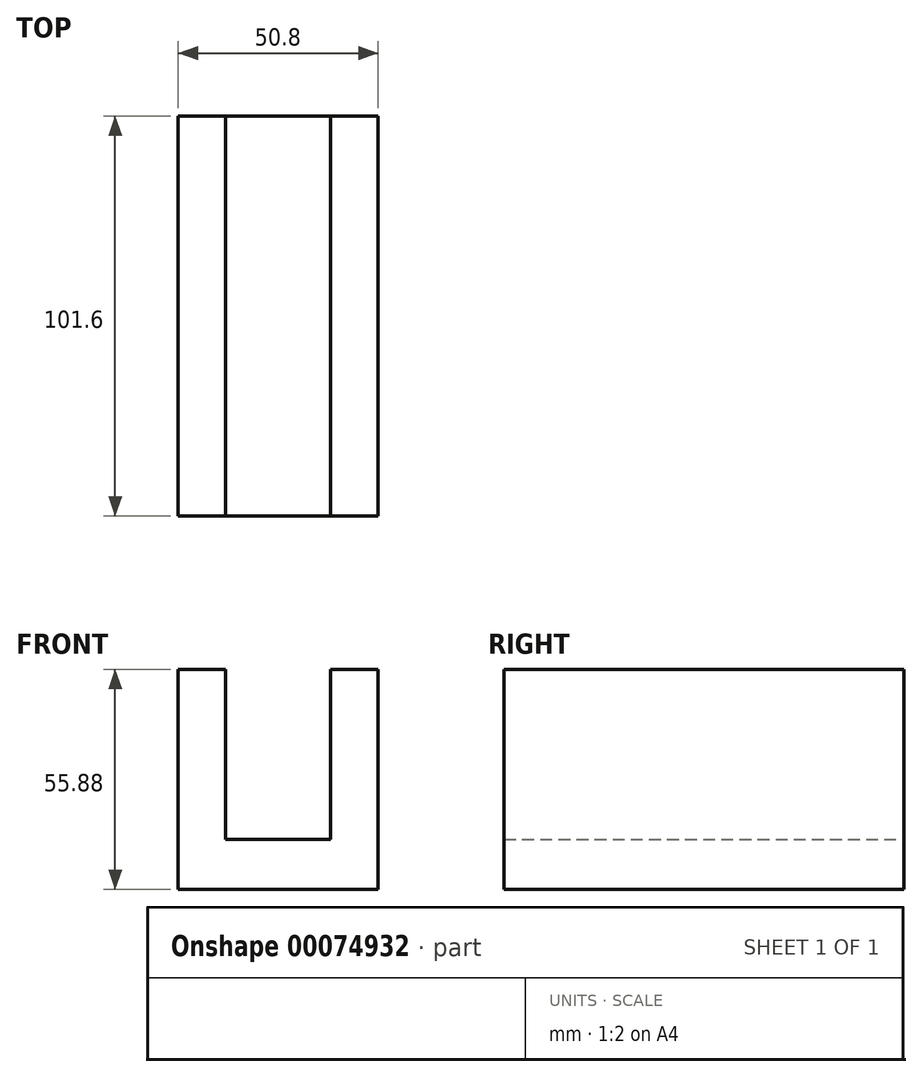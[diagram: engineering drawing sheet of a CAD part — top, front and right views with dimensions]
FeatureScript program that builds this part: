
annotation { "Feature Type Name" : "Feature", "Feature Type Description" : "" }
export const myFeature = defineFeature(function(context is Context, id is Id, definition is map)
    precondition{}
    {
        {
            var Q0;
            Q0=qCreatedBy(makeId("Top.planeOp"),FACE);
            var sketch = newSketch(context, id + "F0", { "sketchPlane" : qUnion([Q0])});
            skLineSegment(sketch, "E0.rect.bottom", {"start": v(25.4, -50.8) * mm, "end": v(-25.4, -50.8) * mm});
            skLineSegment(sketch, "E0.rect.top", {"start": v(25.4, 50.8) * mm, "end": v(-25.4, 50.8) * mm});
            skLineSegment(sketch, "E0.rect.left", {"start": v(25.4, -50.8) * mm, "end": v(25.4, 50.8) * mm});
            skLineSegment(sketch, "E0.rect.right", {"start": v(-25.4, -50.8) * mm, "end": v(-25.4, 50.8) * mm});
            skPoint(sketch, "E0.rect.middle", {"position": v(0, 0) * mm});
            skSolve(sketch);
        }
        {
            var Q0;
            Q0=makeQuery(id+"F0.imprint","IMPRINT",FACE,{"disambiguationData":[TD([[makeQuery(id+"F0.imprint","IMPRINT",EDGE,{"derivedFrom":sQuery(id+"F0.wireOp",EDGE,"E0.rect.bottom")}),-1.0]])]});
            extrude(context, id + "F1", {"entities" : qUnion([Q0]), "endBound" : BoundingType.SYMMETRIC, "depth" : 50.8 * mm});
        }
        {
            var Q0;
            Q0=makeQuery(id+"F1.opExtrude","CAP_FACE",FACE,{"disambiguationData":[OSD([sQuery(id+"F0.wireOp",EDGE,"E0.rect.bottom"),sQuery(id+"F0.wireOp",EDGE,"E0.rect.top"),sQuery(id+"F0.wireOp",EDGE,"E0.rect.left"),sQuery(id+"F0.wireOp",EDGE,"E0.rect.right")])],"isStart":false});
            var sketch = newSketch(context, id + "F2", { "sketchPlane" : qUnion([Q0])});
            skLineSegment(sketch, "E1.rect.bottom", {"start": v(13.33, -50.8) * mm, "end": v(-13.33, -50.8) * mm});
            skLineSegment(sketch, "E1.rect.top", {"start": v(13.33, 50.8) * mm, "end": v(-13.33, 50.8) * mm});
            skLineSegment(sketch, "E1.rect.left", {"start": v(13.33, -50.8) * mm, "end": v(13.33, 50.8) * mm});
            skLineSegment(sketch, "E1.rect.right", {"start": v(-13.33, -50.8) * mm, "end": v(-13.33, 50.8) * mm});
            skPoint(sketch, "E1.rect.middle", {"position": v(0, 0) * mm});
            skSolve(sketch);
        }
        {
            var Q0;
            Q0=makeQuery(id+"F2.imprint","IMPRINT",FACE,{"disambiguationData":[TD([[makeQuery(id+"F2.imprint","IMPRINT",EDGE,{"derivedFrom":sQuery(id+"F2.wireOp",EDGE,"E1.rect.bottom")}),-1.0]])]});
            extrude(context, id + "F3", {"entities" : qUnion([Q0]), "operationType" : NewBodyOperationType.REMOVE, "oppositeDirection" : true, "depth" : 38.1 * mm});
        }
        {
            var Q0;
            {var subQ0=sQuery(id+"F0.wireOp",EDGE,"E0.rect.bottom");var subQ1=sQuery(id+"F0.wireOp",EDGE,"E0.rect.top");var subQ2=sQuery(id+"F0.wireOp",EDGE,"E0.rect.right");Q0=makeQuery(id+"F3.boolean.opBoolean","SPLIT",FACE,{"disambiguationData":[TD([makeQuery(id+"F1.opExtrude","SWEPT_FACE",FACE,{"disambiguationData":[OSD([subQ2])]})])],"derivedFrom":makeQuery(id+"F1.opExtrude","CAP_FACE",FACE,{"disambiguationData":[OSD([subQ0,subQ1,sQuery(id+"F0.wireOp",EDGE,"E0.rect.left"),subQ2])],"isStart":false})});}
            extrude(context, id + "F4", {"entities" : qUnion([Q0]), "operationType" : NewBodyOperationType.ADD, "depth" : 25.4 * mm});
        }
        {
            var Q0;
            {var subQ0=sQuery(id+"F0.wireOp",EDGE,"E0.rect.bottom");var subQ1=sQuery(id+"F0.wireOp",EDGE,"E0.rect.top");var subQ2=sQuery(id+"F0.wireOp",EDGE,"E0.rect.left");Q0=makeQuery(id+"F3.boolean.opBoolean","SPLIT",FACE,{"disambiguationData":[TD([makeQuery(id+"F1.opExtrude","SWEPT_FACE",FACE,{"disambiguationData":[OSD([subQ2])]})])],"derivedFrom":makeQuery(id+"F1.opExtrude","CAP_FACE",FACE,{"disambiguationData":[OSD([subQ0,subQ1,subQ2,sQuery(id+"F0.wireOp",EDGE,"E0.rect.right")])],"isStart":false})});}
            extrude(context, id + "F5", {"entities" : qUnion([Q0]), "operationType" : NewBodyOperationType.ADD, "depth" : 25.4 * mm});
        }
        {
            var Q0;
            Q0=makeQuery(id+"F5.opExtrude","CAP_FACE",FACE,{"disambiguationData":[OSD([sQuery(id+"F0.wireOp",EDGE,"E0.rect.bottom"),sQuery(id+"F0.wireOp",EDGE,"E0.rect.top"),sQuery(id+"F0.wireOp",EDGE,"E0.rect.left"),sQuery(id+"F0.wireOp",EDGE,"E0.rect.right")])],"isStart":false});
            var Q1;
            Q1=makeQuery(id+"F4.opExtrude","CAP_FACE",FACE,{"disambiguationData":[OSD([sQuery(id+"F0.wireOp",EDGE,"E0.rect.bottom"),sQuery(id+"F0.wireOp",EDGE,"E0.rect.top"),sQuery(id+"F0.wireOp",EDGE,"E0.rect.left"),sQuery(id+"F0.wireOp",EDGE,"E0.rect.right")])],"isStart":false});
            extrude(context, id + "F6", {"entities" : qUnion([Q0, Q1]), "operationType" : NewBodyOperationType.REMOVE, "oppositeDirection" : true, "depth" : 20.32 * mm});
        }
    });
